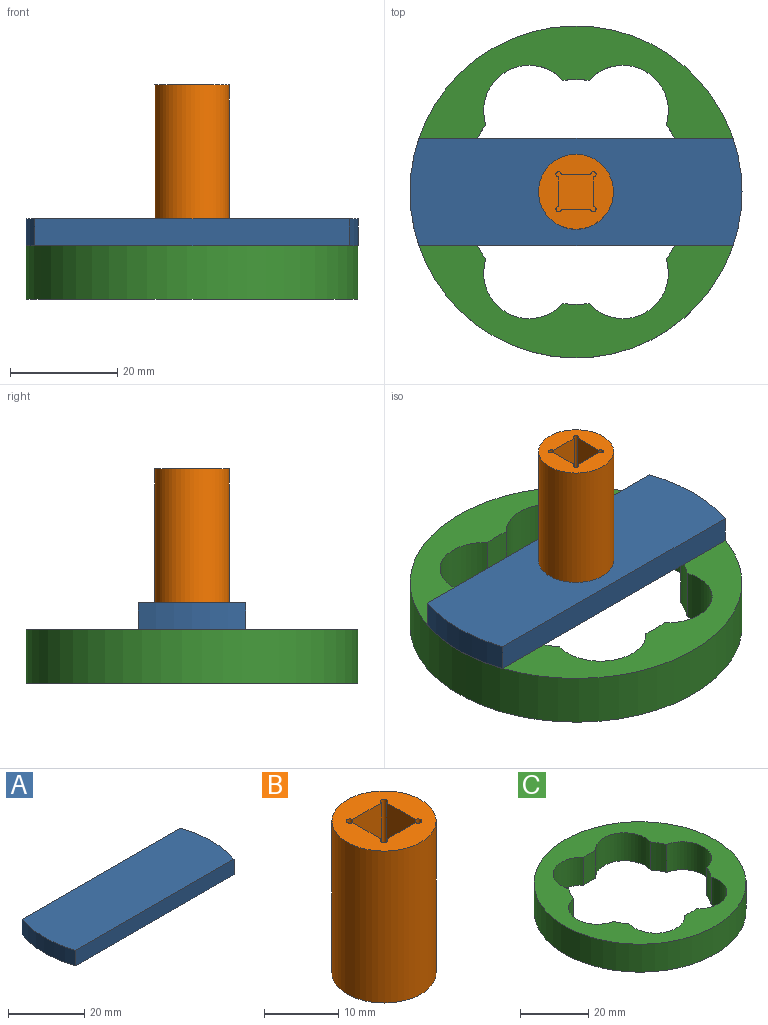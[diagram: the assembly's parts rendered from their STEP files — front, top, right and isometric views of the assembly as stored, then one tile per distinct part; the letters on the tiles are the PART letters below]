
ASSEMBLY  parts=3 mates=2
PART A: 6 faces, bbox 62x20x5 mm
  f0: plane 58.69x5mm, normal (0,1,0), area 293.4mm2, adj f1,f3,f4,f5
  f1: cylinder r=31mm len=20mm, axis (0,0,-1), area 101.8mm2, adj f0,f2,f4,f5
  f2: plane 58.69x5mm, normal (0,-1,0), area 293.4mm2, adj f1,f3,f4,f5
  f3: cylinder r=31mm len=20mm, axis (0,0,-1), area 101.8mm2, adj f0,f2,f4,f5
  f4: plane 62x20mm, normal (0,0,1), area 1218.1mm2, adj f0,f1,f2,f3
  f5: plane 62x20mm, normal (0,0,-1), area 1218.1mm2, adj f0,f1,f2,f3
PART B: 12 faces, bbox 14x14x25 mm
  f0: plane 14x14mm, normal (0,0,1), area 109.3mm2, adj f1,f3,f4,f5,f6,f7,f8,f9
  f1: cylinder r=7mm len=25mm, axis (0,0,-1), area 1099.6mm2, adj f0,f2
  f2: plane 14x14mm, normal (0,0,-1), area 153.9mm2, adj f1
  f3: plane 9x5.5mm, normal (0,1,0), area 49.5mm2, adj f0,f4,f10,f11
  f4: cylinder r=0.5mm len=9mm, axis (0,0,1), area 21.2mm2, adj f0,f3,f5,f11
  f5: plane 9x5.5mm, normal (-1,0,0), area 49.5mm2, adj f0,f4,f6,f11
  f6: cylinder r=0.5mm len=9mm, axis (0,0,1), area 21.2mm2, adj f0,f5,f7,f11
  f7: plane 9x5.5mm, normal (0,-1,0), area 49.5mm2, adj f0,f6,f8,f11
  f8: cylinder r=0.5mm len=9mm, axis (0,0,1), area 21.2mm2, adj f0,f7,f9,f11
  f9: plane 9x5.5mm, normal (1,0,0), area 49.5mm2, adj f0,f8,f10,f11
  f10: cylinder r=0.5mm len=9mm, axis (0,0,1), area 21.2mm2, adj f0,f3,f9,f11
  f11: plane 7.5x7.5mm, normal (0,0,1), area 44.6mm2, adj f3,f4,f5,f6,f7,f8,f9,f10
PART C: 15 faces, bbox 62x62x10 mm
  f0: cylinder r=21mm len=10mm, axis (0,0,-1), area 49mm2, adj f1,f11,f13,f14
  f1: cylinder r=8.5mm len=14.8mm, axis (0,0,-1), area 231.1mm2, adj f0,f2,f13,f14
  f2: cylinder r=21mm len=10mm, axis (0,0,-1), area 49mm2, adj f1,f3,f13,f14
  f3: cylinder r=8.5mm len=14.8mm, axis (0,0,-1), area 231.1mm2, adj f2,f4,f13,f14
  f4: cylinder r=21mm len=10mm, axis (0,0,-1), area 49mm2, adj f3,f5,f13,f14
  f5: cylinder r=8.5mm len=16.62mm, axis (0,0,-1), area 231.1mm2, adj f4,f6,f13,f14
  f6: cylinder r=21mm len=10mm, axis (0,0,-1), area 49mm2, adj f5,f7,f13,f14
  f7: cylinder r=8.5mm len=14.8mm, axis (0,0,-1), area 231.1mm2, adj f6,f8,f13,f14
  f8: cylinder r=21mm len=10mm, axis (0,0,-1), area 49mm2, adj f7,f9,f13,f14
  f9: cylinder r=8.5mm len=14.8mm, axis (0,0,-1), area 231.1mm2, adj f8,f10,f13,f14
  f10: cylinder r=21mm len=10mm, axis (0,0,-1), area 49mm2, adj f9,f11,f13,f14
  f11: cylinder r=8.5mm len=16.62mm, axis (0,0,-1), area 231.1mm2, adj f0,f10,f13,f14
  f12: cylinder r=31mm len=62mm, axis (0,0,-1), area 1947.8mm2, adj f13,f14
  f13: plane 62x62mm, normal (0,0,1), area 1248.4mm2, adj f0,f1,f2,f3,f4,f5,f6,f7
  f14: plane 62x62mm, normal (0,0,-1), area 1248.4mm2, adj f0,f1,f2,f3,f4,f5,f6,f7
PLACE A t=(-12.03,0.5,18.67)mm
PLACE B t=(-12.03,0.5,23.67)mm
PLACE C t=(-12.03,0.5,8.67)mm
MATE fastened A.f1 <-> C.f0  axis (0,0,-1) through (-12.03,0.5,18.67)mm
MATE fastened B.f1 <-> A.f1  axis (0,0,-1) through (-12.03,0.5,23.67)mm
